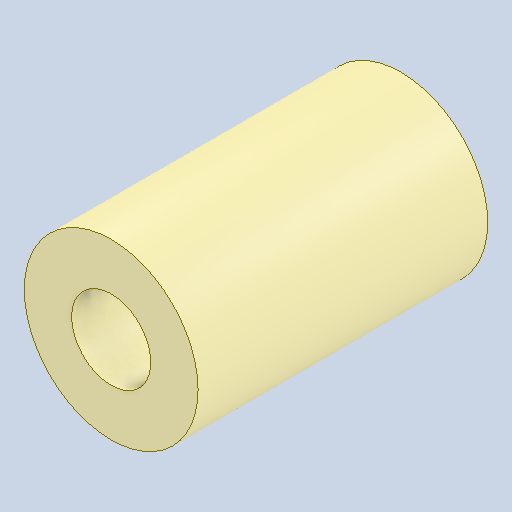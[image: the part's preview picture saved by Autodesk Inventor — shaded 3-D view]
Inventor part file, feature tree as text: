
AUTODESK INVENTOR PART (.ipt)
format: ipt  version: 2023 (Build 270158000, 158)  size: 113,664 bytes
history: native  units: in
note: dims shown in document units (in); Inventor stores cm internally (conversion verified against a paired STEP export)
features: extrude x1
ambient origin geometry x8: Origin, YZ Plane, XZ Plane, XY Plane, X Axis, Y Axis, Z Axis, Center Point
bodies: Solid1 (feature_tree)
feature tree (1):
  extrude  "Extrude1"  [1 undecoded]
note: 1 required parameter value undecoded (feature->parameter linkage not recoverable at this tier; creation-order binding heuristic only, values carry confidence <= 0.55)
